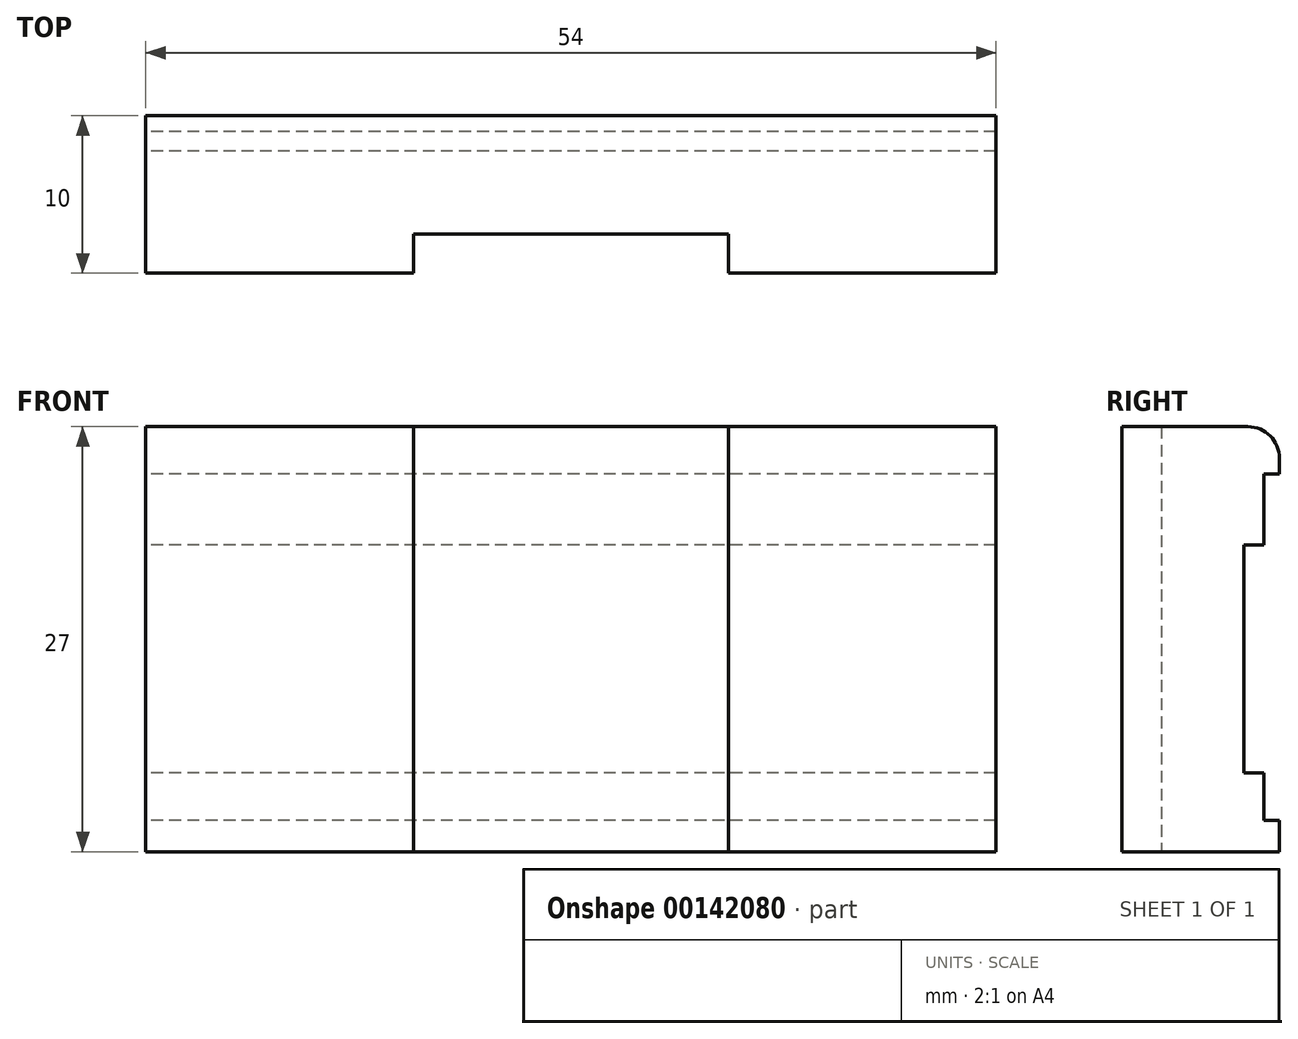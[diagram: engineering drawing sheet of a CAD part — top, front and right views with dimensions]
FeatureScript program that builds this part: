
annotation { "Feature Type Name" : "Feature", "Feature Type Description" : "" }
export const myFeature = defineFeature(function(context is Context, id is Id, definition is map)
    precondition{}
    {
        {
            var Q0;
            Q0=qCreatedBy(makeId("Top.planeOp"),FACE);
            var sketch = newSketch(context, id + "F0", { "sketchPlane" : qUnion([Q0])});
            skLineSegment(sketch, "E0.bottom", {"start": v(27, -5) * mm, "end": v(10, -5) * mm});
            skLineSegment(sketch, "E0.top", {"start": v(27, 5) * mm, "end": v(-27, 5) * mm});
            skLineSegment(sketch, "E0.left", {"start": v(27, -5) * mm, "end": v(27, 5) * mm});
            skLineSegment(sketch, "E0.right", {"start": v(-27, -5) * mm, "end": v(-27, 5) * mm});
            skPoint(sketch, "E0.middle", {"position": v(0, 0) * mm});
            skLineSegment(sketch, "E1", {"start": v(-10, -5) * mm, "end": v(-10, -2.5) * mm});
            skLineSegment(sketch, "E2", {"start": v(-10, -2.5) * mm, "end": v(10, -2.5) * mm});
            skLineSegment(sketch, "E3", {"start": v(10, -2.5) * mm, "end": v(10, -5) * mm});
            skLineSegment(sketch, "E4.trimOffspring", {"start": v(-10, -5) * mm, "end": v(-27, -5) * mm});
            skSolve(sketch);
        }
        {
            var Q0;
            Q0=makeQuery(id+"F0.imprint","IMPRINT",FACE,{"disambiguationData":[TD([[makeQuery(id+"F0.imprint","IMPRINT",EDGE,{"derivedFrom":sQuery(id+"F0.wireOp",EDGE,"E0.bottom")}),-1.0]])]});
            extrude(context, id + "F1", {"entities" : qUnion([Q0]), "depth" : 27 * mm});
        }
        {
            var Q0;
            Q0=makeQuery(id+"F1.opExtrude","SWEPT_FACE",FACE,{"disambiguationData":[OSD([sQuery(id+"F0.wireOp",EDGE,"E0.right")])]});
            var sketch = newSketch(context, id + "F2", { "sketchPlane" : qUnion([Q0])});
            skLineSegment(sketch, "E5.0", {"start": v(-5, 27) * mm, "end": v(-5, 0) * mm});
            skLineSegment(sketch, "E6", {"start": v(-5, 5) * mm, "end": v(-2.75, 5) * mm});
            skLineSegment(sketch, "E7", {"start": v(-2.75, 5) * mm, "end": v(-2.75, 19.5) * mm});
            skLineSegment(sketch, "E8", {"start": v(-2.75, 19.5) * mm, "end": v(-5, 19.5) * mm});
            skLineSegment(sketch, "E9.bottom", {"start": v(-5, 2) * mm, "end": v(-4, 2) * mm});
            skLineSegment(sketch, "E9.top", {"start": v(-5, 24) * mm, "end": v(-4, 24) * mm});
            skLineSegment(sketch, "E9.left", {"start": v(-5, 2) * mm, "end": v(-5, 24) * mm});
            skLineSegment(sketch, "E9.right", {"start": v(-4, 2) * mm, "end": v(-4, 24) * mm});
            skSolve(sketch);
        }
        {
            var Q0;
            {var subQ0=sQuery(id+"F2.wireOp",EDGE,"E6");Q0=makeQuery(id+"F2.imprint","IMPRINT",FACE,{"disambiguationData":[TD([[makeQuery(id+"F2.imprint","IMPRINT",EDGE,{"derivedFrom":subQ0}),1.0]])]});}
            var Q1;
            {var subQ5=sQuery(id+"F2.wireOp",EDGE,"E9.bottom");Q1=makeQuery(id+"F2.imprint","IMPRINT",FACE,{"disambiguationData":[TD([[makeQuery(id+"F2.imprint","IMPRINT",EDGE,{"derivedFrom":subQ5}),1.0]])]});}
            var Q2;
            {var subQ5=sQuery(id+"F2.wireOp",EDGE,"E9.top");Q2=makeQuery(id+"F2.imprint","IMPRINT",FACE,{"disambiguationData":[TD([[makeQuery(id+"F2.imprint","IMPRINT",EDGE,{"derivedFrom":subQ5}),-1.0]])]});}
            extrude(context, id + "F3", {"entities" : qUnion([Q0, Q1, Q2]), "operationType" : NewBodyOperationType.REMOVE, "oppositeDirection" : true, "depth" : 75 * mm});
        }
        {
            var Q0;
            Q0=makeQuery(id+"F1.opExtrude","CAP_EDGE",EDGE,{"disambiguationData":[OSD([sQuery(id+"F0.wireOp",EDGE,"E0.top")])],"isStart":false});
            fillet(context, id + "F4", {"entities" : qUnion([Q0]), "radius" : 2 * mm, "tangentPropagation" : true, "allowEdgeOverflow" : false});
        }
    });
